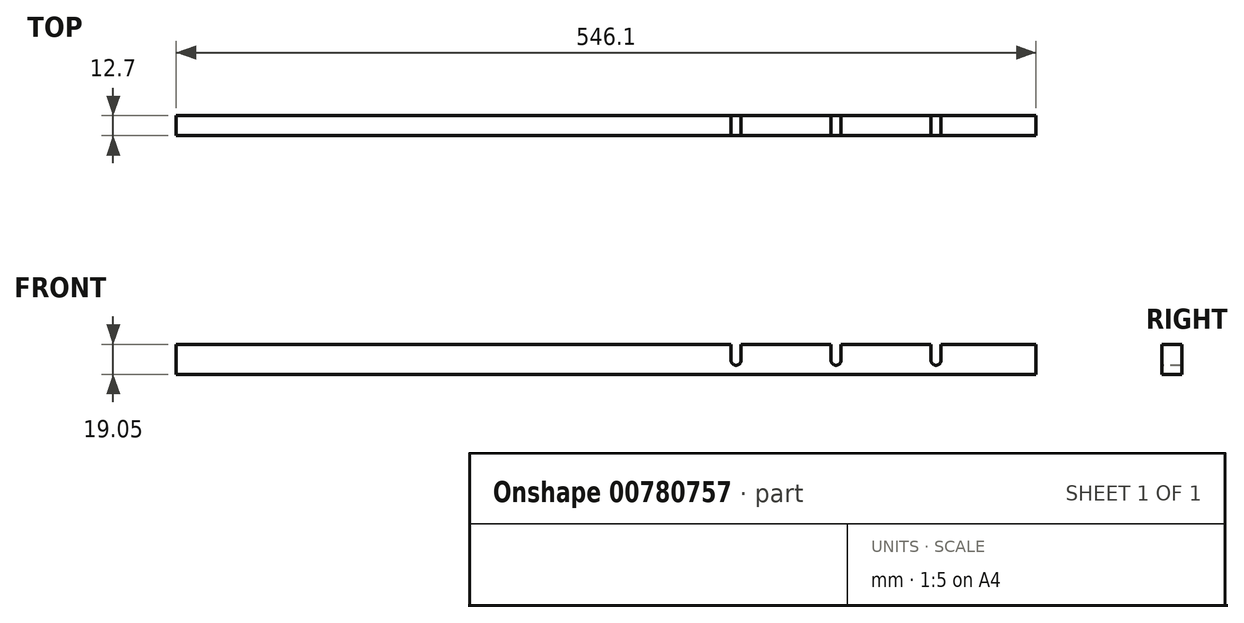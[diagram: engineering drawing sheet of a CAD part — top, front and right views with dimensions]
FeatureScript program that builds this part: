
annotation { "Feature Type Name" : "Feature", "Feature Type Description" : "" }
export const myFeature = defineFeature(function(context is Context, id is Id, definition is map)
    precondition{}
    {
        {
            var Q0;
            Q0=qCreatedBy(makeId("Front.planeOp"),FACE);
            var sketch = newSketch(context, id + "F0", { "sketchPlane" : qUnion([Q0])});
            skLineSegment(sketch, "E0.bottom", {"start": v(-76.14, 12.05) * mm, "end": v(469.96, 12.05) * mm});
            skLineSegment(sketch, "E0.top", {"start": v(-76.14, -7) * mm, "end": v(469.96, -7) * mm});
            skLineSegment(sketch, "E0.left", {"start": v(-76.14, 12.05) * mm, "end": v(-76.14, -7) * mm});
            skLineSegment(sketch, "E0.right", {"start": v(469.96, 12.05) * mm, "end": v(469.96, -7) * mm});
            skSolve(sketch);
        }
        {
            var Q0;
            Q0=makeQuery(id+"F0.imprint","IMPRINT",FACE,{"disambiguationData":[TD([[makeQuery(id+"F0.imprint","IMPRINT",EDGE,{"derivedFrom":sQuery(id+"F0.wireOp",EDGE,"E0.bottom")}),-1.0]])]});
            extrude(context, id + "F1", {"entities" : qUnion([Q0]), "depth" : 12.7 * mm, "offsetDistance" : 25.4 * mm});
        }
        {
            var Q0;
            Q0=makeQuery(id+"F1.opExtrude","CAP_FACE",FACE,{"disambiguationData":[OSD([sQuery(id+"F0.wireOp",EDGE,"E0.bottom"),sQuery(id+"F0.wireOp",EDGE,"E0.top"),sQuery(id+"F0.wireOp",EDGE,"E0.left"),sQuery(id+"F0.wireOp",EDGE,"E0.right")])],"isStart":false});
            var sketch = newSketch(context, id + "F2", { "sketchPlane" : qUnion([Q0])});
            skPoint(sketch, "E1", {"position": v(406.46, 1.89) * mm});
            skPoint(sketch, "E2", {"position": v(342.96, 1.89) * mm});
            skPoint(sketch, "E3", {"position": v(469.96, 1.89) * mm});
            skCircle(sketch, "E4", {"center": v(342.96, 1.89) * mm, "radius": 3.18 * mm});
            skPoint(sketch, "E5", {"position": v(469.96, 12.05) * mm});
            skLineSegment(sketch, "E6", {"start": v(339.79, 1.89) * mm, "end": v(339.79, 12.05) * mm});
            skLineSegment(sketch, "E7", {"start": v(339.79, 12.05) * mm, "end": v(346.14, 12.05) * mm});
            skLineSegment(sketch, "E8", {"start": v(346.14, 12.05) * mm, "end": v(346.14, 1.89) * mm});
            skCircle(sketch, "E9", {"center": v(406.46, 1.89) * mm, "radius": 3.18 * mm});
            skPoint(sketch, "E10", {"position": v(403.29, 12.05) * mm});
            skPoint(sketch, "E11", {"position": v(409.64, 12.05) * mm});
            skPoint(sketch, "E12", {"position": v(409.64, 1.89) * mm});
            skPoint(sketch, "E13", {"position": v(403.29, 1.89) * mm});
            skLineSegment(sketch, "E14", {"start": v(403.29, 12.05) * mm, "end": v(403.29, 1.89) * mm});
            skLineSegment(sketch, "E15", {"start": v(409.64, 12.05) * mm, "end": v(409.64, 1.89) * mm});
            skPoint(sketch, "E16", {"position": v(279.46, 1.89) * mm});
            skCircle(sketch, "E17", {"center": v(279.46, 1.89) * mm, "radius": 3.18 * mm});
            skPoint(sketch, "E18", {"position": v(282.64, 12.05) * mm});
            skPoint(sketch, "E19", {"position": v(276.29, 12.05) * mm});
            skLineSegment(sketch, "E20", {"start": v(282.64, 1.89) * mm, "end": v(282.64, 12.05) * mm});
            skLineSegment(sketch, "E21", {"start": v(276.29, 12.05) * mm, "end": v(276.29, 1.89) * mm});
            skPoint(sketch, "E22", {"position": v(279.46, -7) * mm});
            skSolve(sketch);
        }
        {
            var Q0;
            {var subQ0=sQuery(id+"F2.wireOp",EDGE,"E6");Q0=makeQuery(id+"F2.imprint","IMPRINT",FACE,{"disambiguationData":[TD([[makeQuery(id+"F2.imprint","IMPRINT",EDGE,{"derivedFrom":subQ0}),-1.0]])]});}
            var Q1;
            {var subQ0=sQuery(id+"F2.wireOp",EDGE,"E4");var subQ1=makeQuery(id+"F2.imprint","INTERSECT",VERTEX,{"derivedFrom":[subQ0,sQuery(id+"F2.wireOp",EDGE,"E6")]});Q1=makeQuery(id+"F2.imprint","IMPRINT",FACE,{"disambiguationData":[TD([[makeQuery(id+"F2.imprint","IMPRINT",EDGE,{"disambiguationData":[TD([[subQ1,1.0]])],"derivedFrom":subQ0}),1.0]])]});}
            var Q2;
            {var subQ0=sQuery(id+"F2.wireOp",EDGE,"E14");Q2=makeQuery(id+"F2.imprint","IMPRINT",FACE,{"disambiguationData":[TD([[makeQuery(id+"F2.imprint","IMPRINT",EDGE,{"derivedFrom":subQ0}),1.0]])]});}
            var Q3;
            {var subQ0=sQuery(id+"F2.wireOp",EDGE,"E9");var subQ1=makeQuery(id+"F2.imprint","INTERSECT",VERTEX,{"derivedFrom":[subQ0,sQuery(id+"F2.wireOp",EDGE,"E15")]});Q3=makeQuery(id+"F2.imprint","IMPRINT",FACE,{"disambiguationData":[TD([[makeQuery(id+"F2.imprint","IMPRINT",EDGE,{"disambiguationData":[TD([[subQ1,-1.0]])],"derivedFrom":subQ0}),1.0]])]});}
            var Q4;
            {var subQ0=sQuery(id+"F2.wireOp",EDGE,"E15");Q4=makeQuery(id+"F2.imprint","IMPRINT",FACE,{"disambiguationData":[TD([[makeQuery(id+"F2.imprint","IMPRINT",EDGE,{"derivedFrom":subQ0}),-1.0]])]});}
            var Q5;
            {var subQ0=sQuery(id+"F2.wireOp",EDGE,"E8");Q5=makeQuery(id+"F2.imprint","IMPRINT",FACE,{"disambiguationData":[TD([[makeQuery(id+"F2.imprint","IMPRINT",EDGE,{"derivedFrom":subQ0}),-1.0]])]});}
            var Q6;
            {var subQ0=sQuery(id+"F2.wireOp",EDGE,"E17");var subQ1=makeQuery(id+"F1.opExtrude","CAP_EDGE",EDGE,{"disambiguationData":[OSD([sQuery(id+"F0.wireOp",EDGE,"E0.bottom")])],"isStart":false});var subQ2=makeQuery(id+"F2.imprint","INTERSECT",VERTEX,{"disambiguationData":[OD(0.0)],"derivedFrom":[subQ1,subQ0]});Q6=makeQuery(id+"F2.imprint","IMPRINT",FACE,{"disambiguationData":[TD([[makeQuery(id+"F2.imprint","IMPRINT",EDGE,{"disambiguationData":[TD([[subQ2,-1.0]])],"derivedFrom":subQ0}),1.0]])]});}
            var Q7;
            {var subQ0=sQuery(id+"F2.wireOp",EDGE,"E17");var subQ1=makeQuery(id+"F2.imprint","INTERSECT",VERTEX,{"derivedFrom":[subQ0,sQuery(id+"F2.wireOp",EDGE,"E20")]});Q7=makeQuery(id+"F2.imprint","IMPRINT",FACE,{"disambiguationData":[TD([[makeQuery(id+"F2.imprint","IMPRINT",EDGE,{"disambiguationData":[TD([[subQ1,-1.0]])],"derivedFrom":subQ0}),1.0]])]});}
            var Q8;
            {var subQ0=sQuery(id+"F2.wireOp",EDGE,"E20");Q8=makeQuery(id+"F2.imprint","IMPRINT",FACE,{"disambiguationData":[TD([[makeQuery(id+"F2.imprint","IMPRINT",EDGE,{"derivedFrom":subQ0}),1.0]])]});}
            var Q9;
            {var subQ0=sQuery(id+"F2.wireOp",EDGE,"E21");Q9=makeQuery(id+"F2.imprint","IMPRINT",FACE,{"disambiguationData":[TD([[makeQuery(id+"F2.imprint","IMPRINT",EDGE,{"derivedFrom":subQ0}),1.0]])]});}
            extrude(context, id + "F3", {"entities" : qUnion([Q0, Q1, Q2, Q3, Q4, Q5, Q6, Q7, Q8, Q9]), "operationType" : NewBodyOperationType.REMOVE, "oppositeDirection" : true, "depth" : 25.4 * mm, "offsetDistance" : 25.4 * mm});
        }
    });
